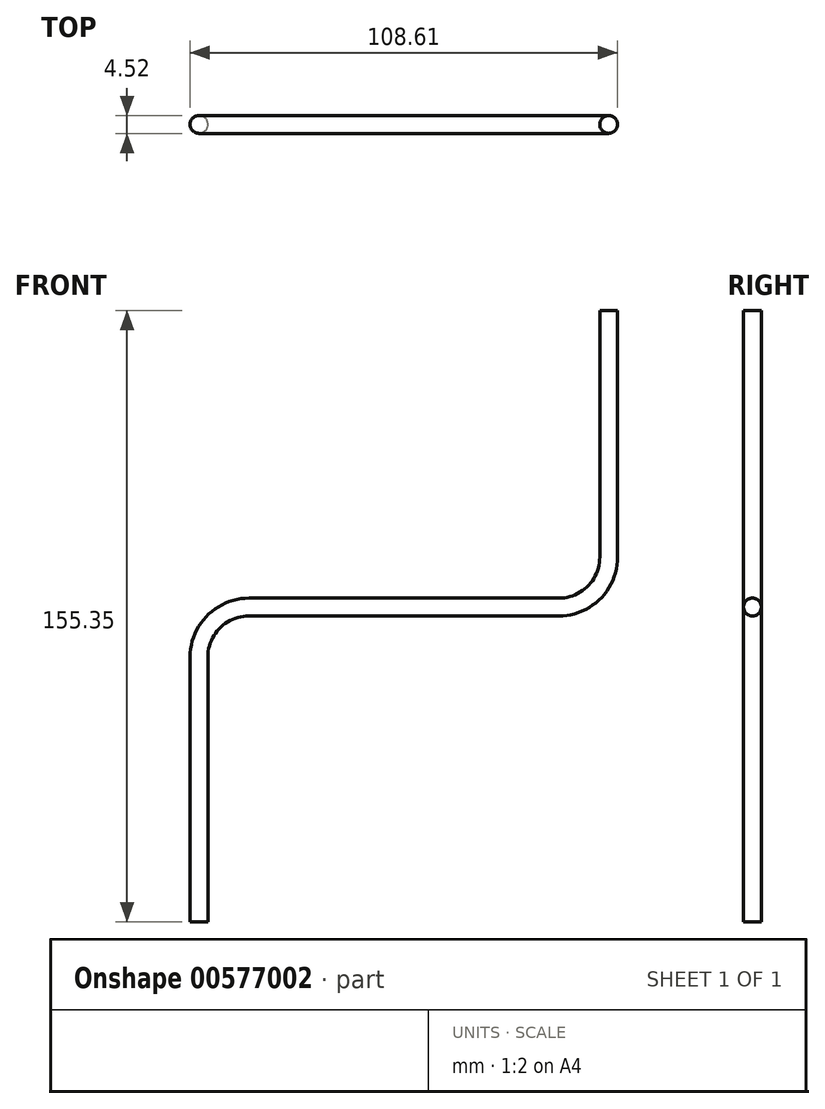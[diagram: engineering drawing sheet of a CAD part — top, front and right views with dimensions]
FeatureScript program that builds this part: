
annotation { "Feature Type Name" : "Feature", "Feature Type Description" : "" }
export const myFeature = defineFeature(function(context is Context, id is Id, definition is map)
    precondition{}
    {
        {
            var Q0;
            Q0=qCreatedBy(makeId("Front.planeOp"),FACE);
            var sketch = newSketch(context, id + "F0", { "sketchPlane" : qUnion([Q0])});
            skLineSegment(sketch, "E0", {"start": v(0, 0) * mm, "end": v(0, 67.3) * mm});
            skLineSegment(sketch, "E1", {"start": v(12.7, 80) * mm, "end": v(91.38, 80) * mm});
            skLineSegment(sketch, "E2", {"start": v(104.08, 92.7) * mm, "end": v(104.08, 155.35) * mm});
            skLineSegment(sketch, "E3", {"start": v(116.78, 168.05) * mm, "end": v(199.38, 168.05) * mm});
            skPoint(sketch, "E4.visualSharp", {"position": v(0, 80) * mm});
            skArc(sketch, "E4.filletArc", {"start": v(12.7, 80) * mm, "mid": v(3.72, 76.28) * mm, "end": v(0, 67.3) * mm});
            skPoint(sketch, "E5.visualSharp", {"position": v(104.08, 80) * mm});
            skArc(sketch, "E5.filletArc", {"start": v(91.38, 80) * mm, "mid": v(100.37, 83.72) * mm, "end": v(104.08, 92.7) * mm});
            skPoint(sketch, "E6.visualSharp", {"position": v(104.08, 168.05) * mm});
            skArc(sketch, "E6.filletArc", {"start": v(116.78, 168.05) * mm, "mid": v(107.8, 164.33) * mm, "end": v(104.08, 155.35) * mm});
            skSolve(sketch);
        }
        {
            var Q0;
            Q0=qCreatedBy(makeId("Top.planeOp"),FACE);
            var sketch = newSketch(context, id + "F1", { "sketchPlane" : qUnion([Q0])});
            skCircle(sketch, "E7", {"center": v(0, 0) * mm, "radius": 2.26 * mm});
            skSolve(sketch);
        }
        {
            var Q0;
            Q0=makeQuery(id+"F1.imprint","IMPRINT",FACE,{"disambiguationData":[TD([[makeQuery(id+"F1.imprint","IMPRINT",EDGE,{"derivedFrom":sQuery(id+"F1.wireOp",EDGE,"E7")}),1.0]])]});
            var Q1;
            Q1=sQuery(id+"F0.wireOp",EDGE,"E0");
            var Q2;
            Q2=sQuery(id+"F0.wireOp",EDGE,"E4.filletArc");
            var Q3;
            Q3=sQuery(id+"F0.wireOp",EDGE,"E1");
            var Q4;
            Q4=sQuery(id+"F0.wireOp",EDGE,"E5.filletArc");
            var Q5;
            Q5=sQuery(id+"F0.wireOp",EDGE,"E2");
            sweep(context, id + "F2", {"profiles" : qUnion([Q0]), "path" : qUnion([Q1, Q2, Q3, Q4, Q5])});
        }
    });
